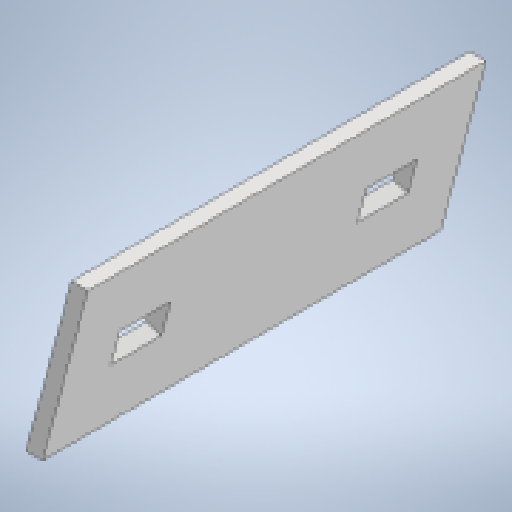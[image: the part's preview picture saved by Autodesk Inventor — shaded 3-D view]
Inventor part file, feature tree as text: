
AUTODESK INVENTOR PART (.ipt)
format: ipt  version: 2023 (Build 270158000, 158)  size: 179,200 bytes
history: native  units: in
note: dims shown in document units (in); Inventor stores cm internally (conversion verified against a paired STEP export)
features: reference x11, other x8, sketch x5, extrude x4, hole x1, projected_geometry x1
ambient origin geometry x8: Origin, YZ Plane, XZ Plane, XY Plane, X Axis, Y Axis, Z Axis, Center Point
bodies: Body1 (feature_tree)
feature tree (30):
  other  "Bryła1"
  extrude  "Wyciągnięcie proste1"  Depth=0.0787in
  extrude  "Wyciągnięcie proste2"  TaperAngle=75.0deg  [1 undecoded]
  extrude  "Wyciągnięcie proste3"  Depth=0.0787in
  extrude  "Wyciągnięcie proste4"  Depth=0.7874in
  hole  "Otwór1"  [1 undecoded]
  sketch  "Szkic1"
  reference  "Odniesienie1"
  sketch  "Szkic2"
  reference  "Odniesienie2"
  reference  "Odniesienie3"
  reference  "Odniesienie4"
  reference  "Odniesienie5"
  sketch  "Szkic3"
  projected_geometry  "Pętla rzutowana1"
  reference  "Odniesienie6"
  sketch  "Szkic4"
  reference  "Odniesienie7"
  reference  "Odniesienie8"
  sketch  "Szkic5"
  reference  "Odniesienie9"
  reference  "Odniesienie10"
  reference  "Odniesienie11"
  other  "<userpath>\Documents\PROJECTS - repos\Stratos---MicroSumo\mechanics\byk_alternator.iam"
  other  "byk_alternator.iam"
  other  "podstawa:1"
  other  "<userpath>\Documents\Inventor\MikroNalesnik\byk_alternator.iam"
  other  "TOF_VL53L0X (1):2"
  other  "TOF_VL53L0X (1):1"
  other  "dach:1"
note: 2 required parameter values undecoded (feature->parameter linkage not recoverable at this tier; creation-order binding heuristic only, values carry confidence <= 0.55)
